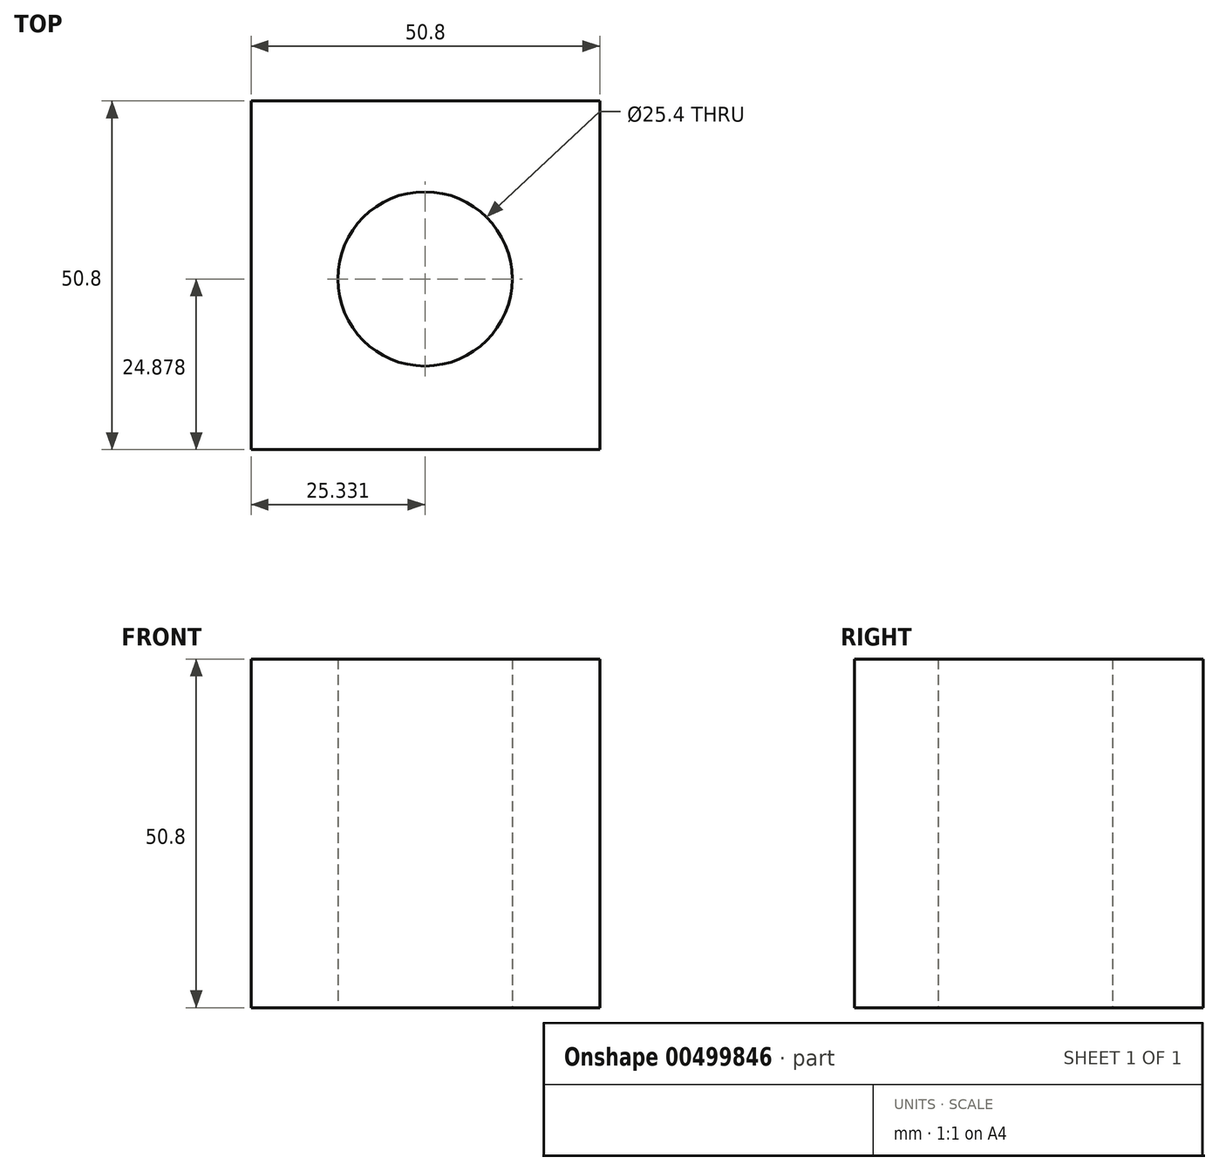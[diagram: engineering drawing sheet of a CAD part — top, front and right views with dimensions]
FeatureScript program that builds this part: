
annotation { "Feature Type Name" : "Feature", "Feature Type Description" : "" }
export const myFeature = defineFeature(function(context is Context, id is Id, definition is map)
    precondition{}
    {
        {
            var Q0;
            Q0=qCreatedBy(makeId("Top.planeOp"),FACE);
            var sketch = newSketch(context, id + "F0", { "sketchPlane" : qUnion([Q0])});
            skLineSegment(sketch, "E0.bottom", {"start": v(-50.8, 50.8) * mm, "end": v(0, 50.8) * mm});
            skLineSegment(sketch, "E0.top", {"start": v(-50.8, 0) * mm, "end": v(0, 0) * mm});
            skLineSegment(sketch, "E0.left", {"start": v(-50.8, 50.8) * mm, "end": v(-50.8, 0) * mm});
            skLineSegment(sketch, "E0.right", {"start": v(0, 50.8) * mm, "end": v(0, 0) * mm});
            skSolve(sketch);
        }
        {
            var Q0;
            Q0=makeQuery(id+"F0.imprint","IMPRINT",FACE,{"disambiguationData":[TD([[makeQuery(id+"F0.imprint","IMPRINT",EDGE,{"derivedFrom":sQuery(id+"F0.wireOp",EDGE,"E0.bottom")}),-1.0]])]});
            extrude(context, id + "F1", {"entities" : qUnion([Q0]), "depth" : 50.8 * mm});
        }
        {
            var Q0;
            Q0=qCreatedBy(makeId("Top.planeOp"),FACE);
            var sketch = newSketch(context, id + "F2", { "sketchPlane" : qUnion([Q0])});
            skCircle(sketch, "E1", {"center": v(-25.47, 24.88) * mm, "radius": 14.98 * mm});
            skSolve(sketch);
        }
        {
            var Q0;
            Q0=sQuery(id+"F2.wireOp",VERTEX,"E1.center");
            var Q1;
            Q1=makeQuery(id+"F1.opExtrude","SWEPT_BODY",BODY,{"disambiguationData":[OSD([sQuery(id+"F0.wireOp",EDGE,"E0.bottom"),sQuery(id+"F0.wireOp",EDGE,"E0.top"),sQuery(id+"F0.wireOp",EDGE,"E0.left"),sQuery(id+"F0.wireOp",EDGE,"E0.right")])]});
            hole(context, id + "F3", {"style" : HoleStyle.SIMPLE, "endStyle" : HoleEndStyle.THROUGH, "oppositeDirection" : true, "holeDiameter" : 25.4 * mm, "isTappedThrough" : true, "tappedDepth" : 12.7 * mm, "tapClearance" : 3, "locations" : qUnion([Q0]), "scope" : qUnion([Q1])});
        }
    });
